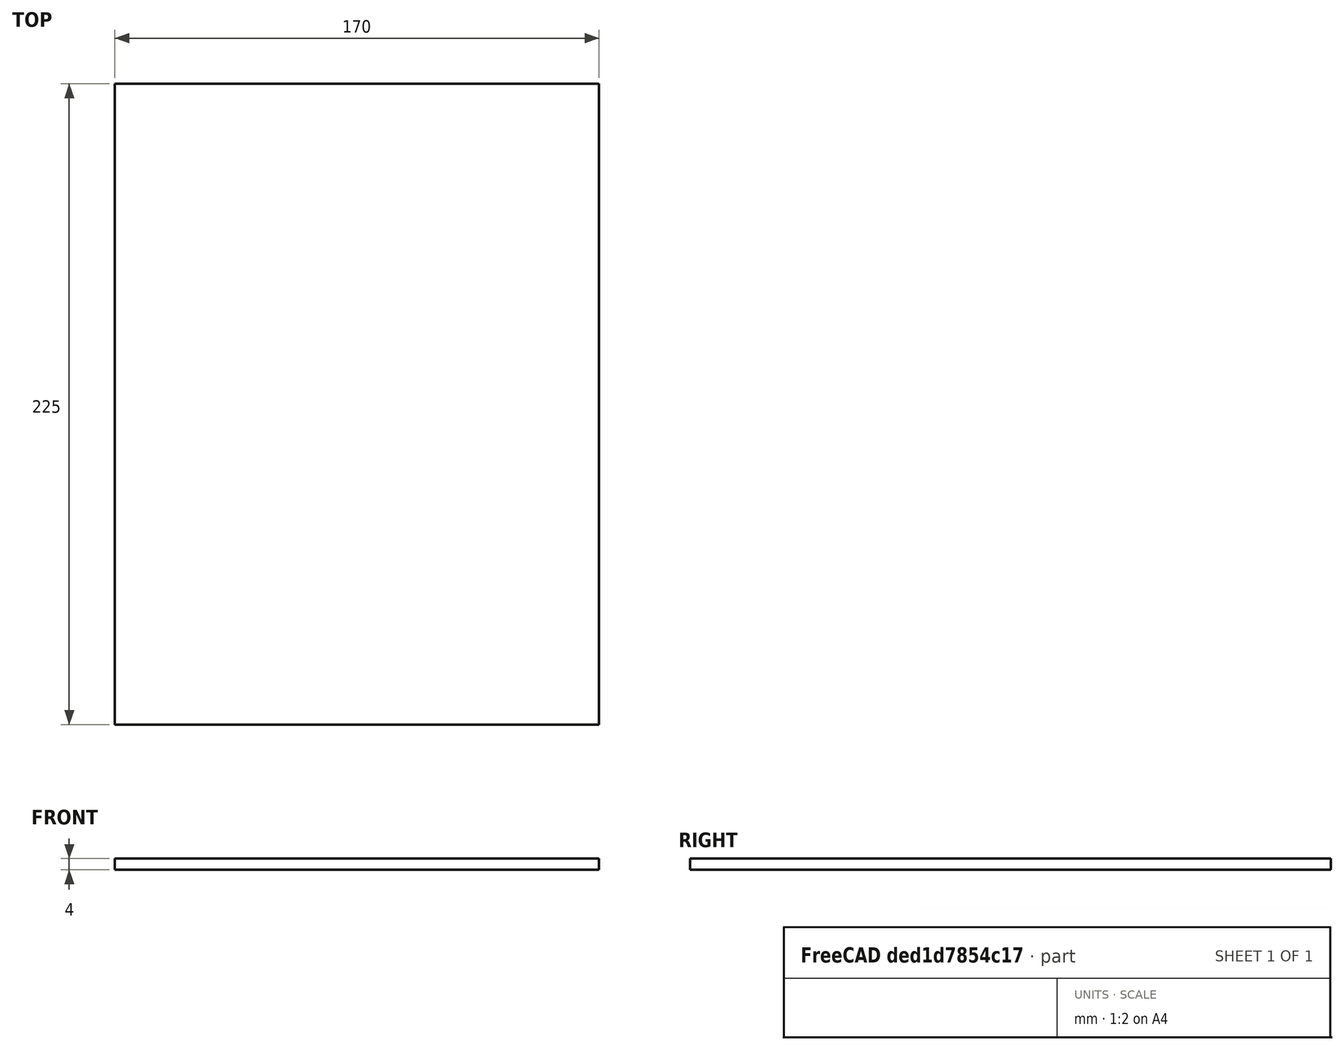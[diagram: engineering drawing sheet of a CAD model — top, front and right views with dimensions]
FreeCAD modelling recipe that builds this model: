
FCSTD DOCUMENT  (FreeCAD 0.17R13528 (Git))
Label: main_glass
License: All rights reserved
LicenseURL: http://en.wikipedia.org/wiki/All_rights_reserved
objects: Sketcher::SketchObject×1, PartDesign::Pad×1, PartDesign::Body×1
note: 4 computed .brp shape members not serialized (recipe doc carries the construction recipe); baked Part::Feature solids carry a one-line shape summary decoded from their .brp

FEATURE [Sketcher::SketchObject] Sketch
  MapMode = 5
  Support = -> [XY_Plane]
  sketch-geometry (4):
    g0: LineSegment StartX=0 StartY=0 StartZ=0 EndX=-170 EndY=0 EndZ=0
    g1: LineSegment StartX=-170 StartY=0 StartZ=0 EndX=-170 EndY=225 EndZ=0
    g2: LineSegment StartX=-170 StartY=225 StartZ=0 EndX=0 EndY=225 EndZ=0
    g3: LineSegment StartX=0 StartY=225 StartZ=0 EndX=0 EndY=0 EndZ=0
  constraints (11):
    c: Coincident(g0,g1)
    c: Coincident(g1,g2)
    c: Coincident(g2,g3)
    c: Coincident(g3,g0)
    c: Horizontal(g0)
    c: Horizontal(g2)
    c: Vertical(g1)
    c: Vertical(g3)
    c: Coincident(g0,g-1)
    c: DistanceY(g1,g1) = 225  'height'
    c: DistanceX(g2,g2) = 170  'width'
FEATURE [PartDesign::Pad] Pad
  Length = 4
  Length2 = 100
  Profile = -> Sketch
  Type = 0
FEATURE [PartDesign::Body] Body
  Group = -> [Sketch,Pad]
  Origin = -> Origin
  Tip = -> Pad
